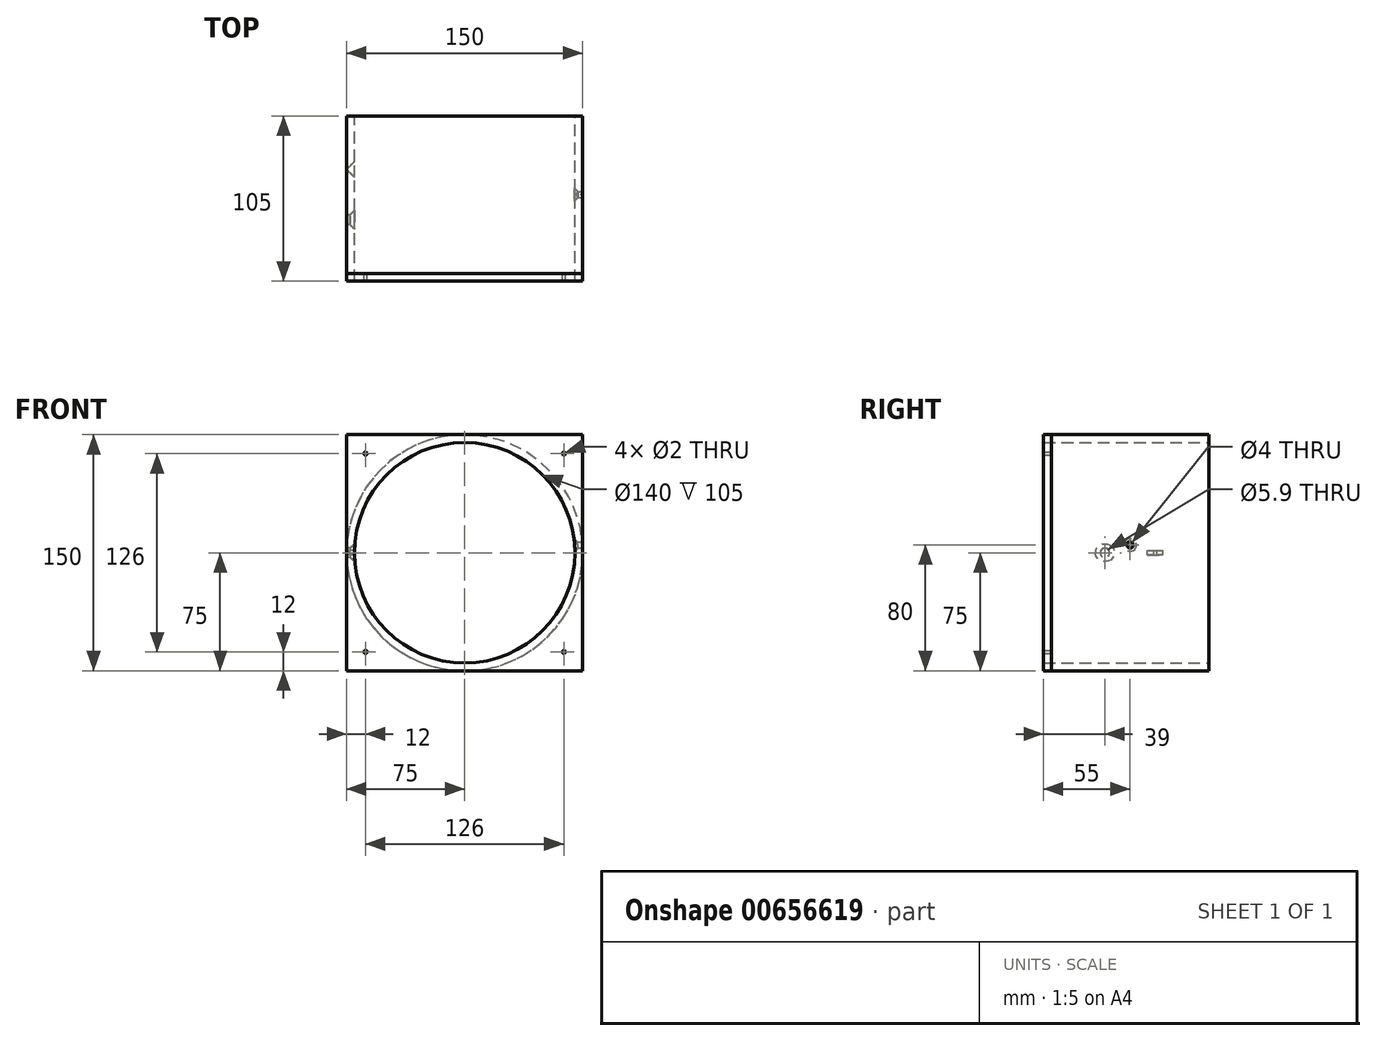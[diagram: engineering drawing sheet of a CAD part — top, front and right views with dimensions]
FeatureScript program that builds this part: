
annotation { "Feature Type Name" : "Feature", "Feature Type Description" : "" }
export const myFeature = defineFeature(function(context is Context, id is Id, definition is map)
    precondition{}
    {
        {
            var Q0;
            Q0=qCreatedBy(makeId("Front.planeOp"),FACE);
            var sketch = newSketch(context, id + "F0", { "sketchPlane" : qUnion([Q0])});
            skCircle(sketch, "E0", {"center": v(0, 0) * mm, "radius": 70 * mm});
            skCircle(sketch, "E1", {"center": v(0, 0) * mm, "radius": 75 * mm});
            skSolve(sketch);
        }
        {
            var Q0;
            Q0 = qSketchRegion(id + "F0", true);
            extrude(context, id + "F1", {"entities" : qUnion([Q0]), "depth" : 100 * mm, "offsetDistance" : 25 * mm});
        }
        {
            var Q0;
            Q0=makeQuery(id+"F1.opExtrude","CAP_FACE",FACE,{"disambiguationData":[OSD([sQuery(id+"F0.wireOp",EDGE,"E0"),sQuery(id+"F0.wireOp",EDGE,"E1")])],"isStart":false});
            var sketch = newSketch(context, id + "F2", { "sketchPlane" : qUnion([Q0])});
            skLineSegment(sketch, "E2.bottom", {"start": v(-75, 75) * mm, "end": v(75, 75) * mm});
            skLineSegment(sketch, "E2.top", {"start": v(-75, -75) * mm, "end": v(75, -75) * mm});
            skLineSegment(sketch, "E2.left", {"start": v(-75, 75) * mm, "end": v(-75, -75) * mm});
            skLineSegment(sketch, "E2.right", {"start": v(75, 75) * mm, "end": v(75, -75) * mm});
            skCircle(sketch, "E3", {"center": v(0, 0) * mm, "radius": 70 * mm});
            skCircle(sketch, "E4", {"center": v(-63, 63) * mm, "radius": 1 * mm});
            skCircle(sketch, "E5", {"center": v(63, 63) * mm, "radius": 1 * mm});
            skCircle(sketch, "E6", {"center": v(63, -63) * mm, "radius": 1 * mm});
            skCircle(sketch, "E7", {"center": v(-63, -63) * mm, "radius": 1 * mm});
            skSolve(sketch);
        }
        {
            var Q0;
            Q0 = qSketchRegion(id + "F2", true);
            extrude(context, id + "F3", {"entities" : qUnion([Q0]), "operationType" : NewBodyOperationType.ADD, "depth" : 5 * mm, "offsetDistance" : 25 * mm});
        }
        {
            var Q0;
            Q0=makeQuery(id+"F3.opExtrude","SWEPT_FACE",FACE,{"disambiguationData":[OSD([sQuery(id+"F2.wireOp",EDGE,"E2.right")])]});
            var sketch = newSketch(context, id + "F4", { "sketchPlane" : qUnion([Q0])});
            skCircle(sketch, "E8", {"center": v(-50, 5) * mm, "radius": 2 * mm});
            skSolve(sketch);
        }
        {
            var Q0;
            Q0 = qSketchRegion(id + "F4", true);
            extrude(context, id + "F5", {"entities" : qUnion([Q0]), "operationType" : NewBodyOperationType.REMOVE, "oppositeDirection" : true, "depth" : 25 * mm, "offsetDistance" : 25 * mm});
        }
        {
            var Q0;
            Q0=makeQuery(id+"F3.opExtrude","SWEPT_FACE",FACE,{"disambiguationData":[OSD([sQuery(id+"F2.wireOp",EDGE,"E2.left")])]});
            var sketch = newSketch(context, id + "F6", { "sketchPlane" : qUnion([Q0])});
            skLineSegment(sketch, "E9.bottom", {"start": v(33, 1.5) * mm, "end": v(35, 1.5) * mm});
            skLineSegment(sketch, "E9.top", {"start": v(33, -1.5) * mm, "end": v(35, -1.5) * mm});
            skLineSegment(sketch, "E9.left", {"start": v(33, 1.5) * mm, "end": v(33, -1.5) * mm});
            skLineSegment(sketch, "E9.right", {"start": v(35, 1.5) * mm, "end": v(35, -1.5) * mm});
            skCircle(sketch, "E10", {"center": v(66, 0) * mm, "radius": 2.95 * mm});
            skSolve(sketch);
        }
        {
            var Q0;
            Q0 = qSketchRegion(id + "F6", true);
            extrude(context, id + "F7", {"entities" : qUnion([Q0]), "operationType" : NewBodyOperationType.REMOVE, "oppositeDirection" : true, "depth" : 25 * mm, "offsetDistance" : 25 * mm});
        }
        {
            var Q0;
            Q0=makeQuery(id+"F7.boolean.opBoolean","INTERSECT",EDGE,{"derivedFrom":[makeQuery(id+"F3.boolean.opBoolean","MERGE",FACE,{"derivedFrom":[makeQuery(id+"F1.opExtrude","SWEPT_FACE",FACE,{"disambiguationData":[OSD([sQuery(id+"F0.wireOp",EDGE,"E0")])]}),makeQuery(id+"F3.opExtrude","SWEPT_FACE",FACE,{"disambiguationData":[OSD([sQuery(id+"F2.wireOp",EDGE,"E3")])]})]}),makeQuery(id+"F7.opExtrude","SWEPT_FACE",FACE,{"disambiguationData":[OSD([sQuery(id+"F6.wireOp",EDGE,"E10")])]})]});
            chamfer(context, id + "F8", {"entities" : qUnion([Q0]), "width" : 3 * mm, "tangentPropagation" : true});
        }
        {
            var Q0;
            Q0=makeQuery(id+"F5.boolean.opBoolean","INTERSECT",EDGE,{"derivedFrom":[makeQuery(id+"F3.boolean.opBoolean","MERGE",FACE,{"derivedFrom":[makeQuery(id+"F1.opExtrude","SWEPT_FACE",FACE,{"disambiguationData":[OSD([sQuery(id+"F0.wireOp",EDGE,"E0")])]}),makeQuery(id+"F3.opExtrude","SWEPT_FACE",FACE,{"disambiguationData":[OSD([sQuery(id+"F2.wireOp",EDGE,"E3")])]})]}),makeQuery(id+"F5.opExtrude","SWEPT_FACE",FACE,{"disambiguationData":[OSD([sQuery(id+"F4.wireOp",EDGE,"E8")])]})]});
            chamfer(context, id + "F9", {"entities" : qUnion([Q0]), "width" : 2 * mm, "tangentPropagation" : true});
        }
        {
            var Q0;
            Q0=makeQuery(id+"F7.boolean.opBoolean","INTERSECT",EDGE,{"derivedFrom":[makeQuery(id+"F3.boolean.opBoolean","MERGE",FACE,{"derivedFrom":[makeQuery(id+"F1.opExtrude","SWEPT_FACE",FACE,{"disambiguationData":[OSD([sQuery(id+"F0.wireOp",EDGE,"E0")])]}),makeQuery(id+"F3.opExtrude","SWEPT_FACE",FACE,{"disambiguationData":[OSD([sQuery(id+"F2.wireOp",EDGE,"E3")])]})]}),makeQuery(id+"F7.opExtrude","SWEPT_FACE",FACE,{"disambiguationData":[OSD([sQuery(id+"F6.wireOp",EDGE,"E9.right")])]})]});
            var Q1;
            Q1=makeQuery(id+"F7.boolean.opBoolean","INTERSECT",EDGE,{"derivedFrom":[makeQuery(id+"F3.boolean.opBoolean","MERGE",FACE,{"derivedFrom":[makeQuery(id+"F1.opExtrude","SWEPT_FACE",FACE,{"disambiguationData":[OSD([sQuery(id+"F0.wireOp",EDGE,"E0")])]}),makeQuery(id+"F3.opExtrude","SWEPT_FACE",FACE,{"disambiguationData":[OSD([sQuery(id+"F2.wireOp",EDGE,"E3")])]})]}),makeQuery(id+"F7.opExtrude","SWEPT_FACE",FACE,{"disambiguationData":[OSD([sQuery(id+"F6.wireOp",EDGE,"E9.left")])]})]});
            chamfer(context, id + "F10", {"entities" : qUnion([Q0, Q1]), "width" : 4 * mm, "tangentPropagation" : true});
        }
    });
